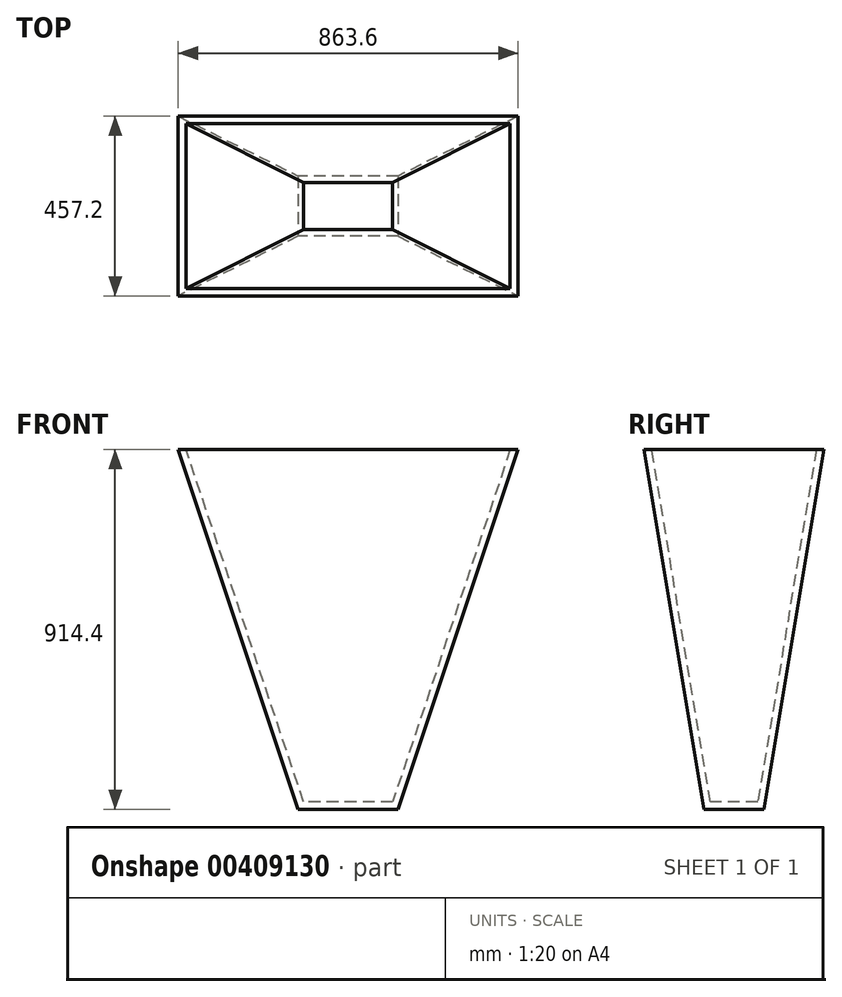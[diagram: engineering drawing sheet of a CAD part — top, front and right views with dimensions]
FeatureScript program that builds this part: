
annotation { "Feature Type Name" : "Feature", "Feature Type Description" : "" }
export const myFeature = defineFeature(function(context is Context, id is Id, definition is map)
    precondition{}
    {
        {
            var Q0;
            Q0=qCreatedBy(makeId("Front.planeOp"),FACE);
            var sketch = newSketch(context, id + "F0", { "sketchPlane" : qUnion([Q0])});
            skLineSegment(sketch, "E0.bottom", {"start": v(431.8, 457.2) * mm, "end": v(-431.8, 457.2) * mm});
            skLineSegment(sketch, "E0.top", {"start": v(431.8, -457.2) * mm, "end": v(-431.8, -457.2) * mm});
            skLineSegment(sketch, "E0.left", {"start": v(431.8, 457.2) * mm, "end": v(431.8, -457.2) * mm});
            skLineSegment(sketch, "E0.right", {"start": v(-431.8, 457.2) * mm, "end": v(-431.8, -457.2) * mm});
            skPoint(sketch, "E0.middle", {"position": v(0, 0) * mm});
            skSolve(sketch);
        }
        {
            var Q0;
            Q0=makeQuery(id+"F0.imprint","IMPRINT",FACE,{"disambiguationData":[TD([[makeQuery(id+"F0.imprint","IMPRINT",EDGE,{"derivedFrom":sQuery(id+"F0.wireOp",EDGE,"E0.bottom")}),1.0]])]});
            extrude(context, id + "F1", {"entities" : qUnion([Q0]), "endBound" : BoundingType.SYMMETRIC, "depth" : 457.2 * mm});
        }
        {
            var Q0;
            Q0=makeQuery(id+"F1.opExtrude","CAP_FACE",FACE,{"disambiguationData":[OSD([sQuery(id+"F0.wireOp",EDGE,"E0.bottom"),sQuery(id+"F0.wireOp",EDGE,"E0.top"),sQuery(id+"F0.wireOp",EDGE,"E0.left"),sQuery(id+"F0.wireOp",EDGE,"E0.right")])],"isStart":false});
            var sketch = newSketch(context, id + "F2", { "sketchPlane" : qUnion([Q0])});
            skLineSegment(sketch, "E1", {"start": v(431.8, 457.2) * mm, "end": v(431.8, -457.2) * mm});
            skLineSegment(sketch, "E2", {"start": v(431.8, -457.2) * mm, "end": v(127, -457.2) * mm});
            skLineSegment(sketch, "E3", {"start": v(127, -457.2) * mm, "end": v(431.8, 457.2) * mm});
            skLineSegment(sketch, "E4", {"start": v(-431.8, 457.2) * mm, "end": v(-431.8, -457.2) * mm});
            skLineSegment(sketch, "E5", {"start": v(-431.8, -457.2) * mm, "end": v(-127, -457.2) * mm});
            skLineSegment(sketch, "E6", {"start": v(-127, -457.2) * mm, "end": v(-431.8, 457.2) * mm});
            skSolve(sketch);
        }
        {
            var Q0;
            Q0=makeQuery(id+"F1.opExtrude","SWEPT_FACE",FACE,{"disambiguationData":[OSD([sQuery(id+"F0.wireOp",EDGE,"E0.right")])]});
            var sketch = newSketch(context, id + "F3", { "sketchPlane" : qUnion([Q0])});
            skLineSegment(sketch, "E7", {"start": v(-228.6, 457.2) * mm, "end": v(-228.6, -457.2) * mm});
            skLineSegment(sketch, "E8", {"start": v(-228.6, -457.2) * mm, "end": v(-76.2, -457.2) * mm});
            skLineSegment(sketch, "E9", {"start": v(-76.2, -457.2) * mm, "end": v(-228.6, 457.2) * mm});
            skLineSegment(sketch, "E10", {"start": v(228.6, 457.2) * mm, "end": v(76.2, -457.2) * mm});
            skLineSegment(sketch, "E11", {"start": v(76.2, -457.2) * mm, "end": v(228.6, -457.2) * mm});
            skLineSegment(sketch, "E12", {"start": v(228.6, -457.2) * mm, "end": v(228.6, 457.2) * mm});
            skSolve(sketch);
        }
        {
            var Q0;
            Q0=makeQuery(id+"F2.imprint","IMPRINT",FACE,{"disambiguationData":[TD([[makeQuery(id+"F2.imprint","IMPRINT",EDGE,{"derivedFrom":sQuery(id+"F2.wireOp",EDGE,"E4")}),1.0]])]});
            var Q1;
            Q1=makeQuery(id+"F2.imprint","IMPRINT",FACE,{"disambiguationData":[TD([[makeQuery(id+"F2.imprint","IMPRINT",EDGE,{"derivedFrom":sQuery(id+"F2.wireOp",EDGE,"E1")}),-1.0]])]});
            extrude(context, id + "F4", {"entities" : qUnion([Q0, Q1]), "operationType" : NewBodyOperationType.REMOVE, "endBound" : BoundingType.THROUGH_ALL, "oppositeDirection" : true, "depth" : 25.4 * mm});
        }
        {
            var Q0;
            Q0=makeQuery(id+"F3.imprint","IMPRINT",FACE,{"disambiguationData":[TD([[makeQuery(id+"F3.imprint","IMPRINT",EDGE,{"derivedFrom":sQuery(id+"F3.wireOp",EDGE,"E7")}),1.0]])]});
            var Q1;
            Q1=makeQuery(id+"F3.imprint","IMPRINT",FACE,{"disambiguationData":[TD([[makeQuery(id+"F3.imprint","IMPRINT",EDGE,{"derivedFrom":sQuery(id+"F3.wireOp",EDGE,"E10")}),1.0]])]});
            extrude(context, id + "F5", {"entities" : qUnion([Q0, Q1]), "operationType" : NewBodyOperationType.REMOVE, "endBound" : BoundingType.THROUGH_ALL, "oppositeDirection" : true, "depth" : 25.4 * mm});
        }
        {
            var Q0;
            Q0=makeQuery(id+"F1.opExtrude","SWEPT_FACE",FACE,{"disambiguationData":[OSD([sQuery(id+"F0.wireOp",EDGE,"E0.bottom")])]});
            shell(context, id + "F6", {"entities" : qUnion([Q0]), "thickness" : 19.05 * mm});
        }
    });
